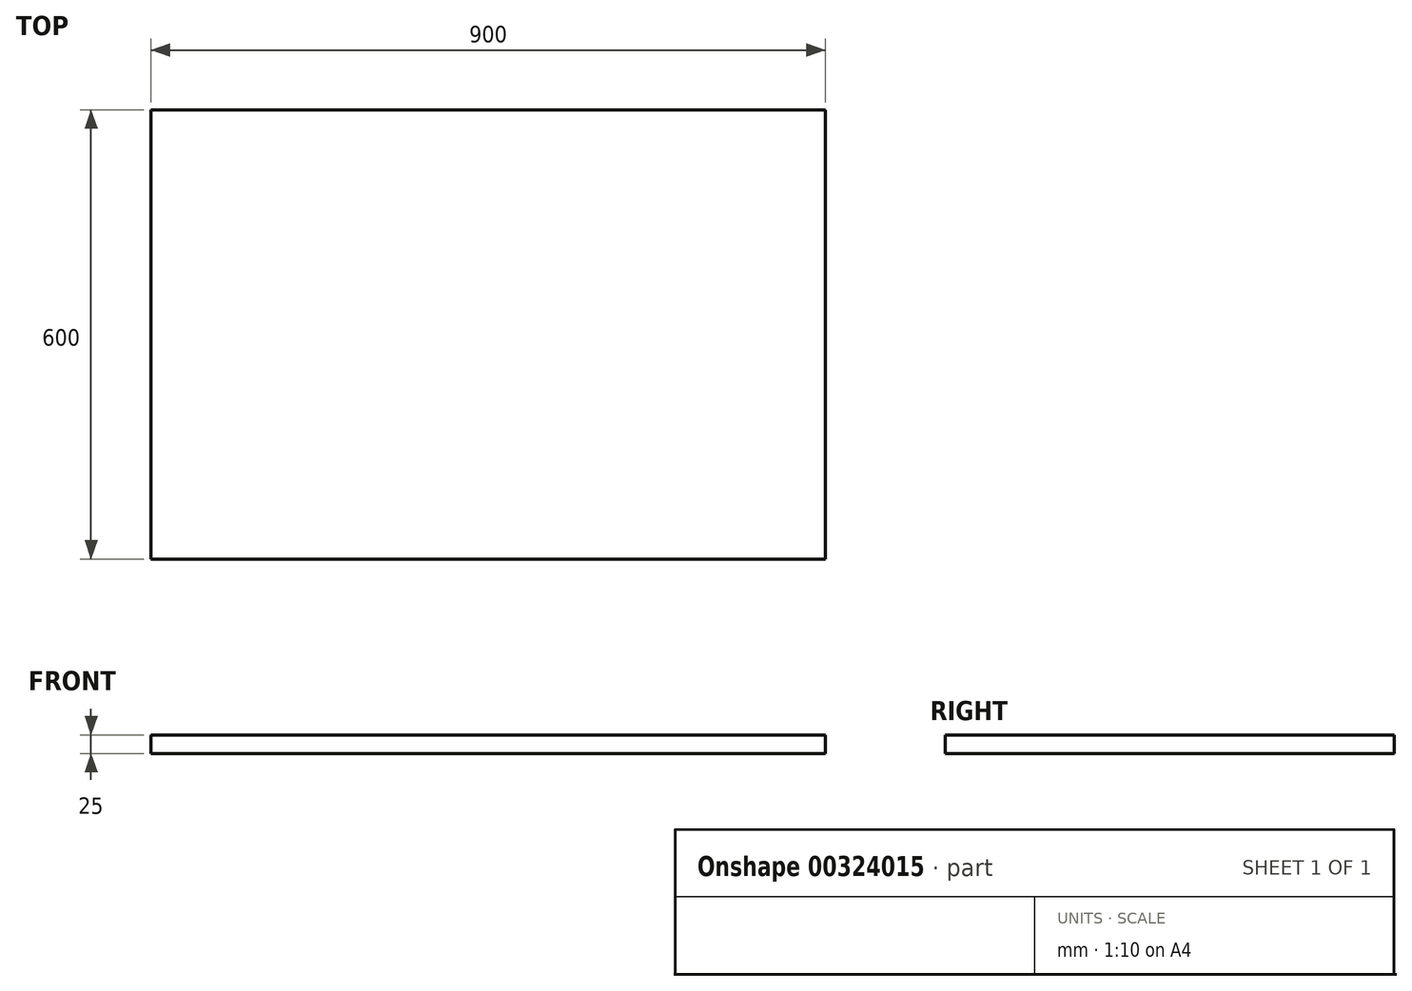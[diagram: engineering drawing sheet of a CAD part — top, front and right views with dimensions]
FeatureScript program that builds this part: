
annotation { "Feature Type Name" : "Feature", "Feature Type Description" : "" }
export const myFeature = defineFeature(function(context is Context, id is Id, definition is map)
    precondition{}
    {
        {
            var Q0;
            Q0=qCreatedBy(makeId("Top.planeOp"),FACE);
            var sketch = newSketch(context, id + "F0", { "sketchPlane" : qUnion([Q0])});
            skLineSegment(sketch, "E0.bottom", {"start": v(450, 300) * mm, "end": v(-450, 300) * mm});
            skLineSegment(sketch, "E0.top", {"start": v(450, -300) * mm, "end": v(-450, -300) * mm});
            skLineSegment(sketch, "E0.left", {"start": v(450, 300) * mm, "end": v(450, -300) * mm});
            skLineSegment(sketch, "E0.right", {"start": v(-450, 300) * mm, "end": v(-450, -300) * mm});
            skPoint(sketch, "E0.middle", {"position": v(0, 0) * mm});
            skSolve(sketch);
        }
        {
            var Q0;
            Q0=makeQuery(id+"F0.imprint","IMPRINT",FACE,{"disambiguationData":[TD([[makeQuery(id+"F0.imprint","IMPRINT",EDGE,{"derivedFrom":sQuery(id+"F0.wireOp",EDGE,"E0.bottom")}),1.0]])]});
            extrude(context, id + "F1", {"entities" : qUnion([Q0]), "depth" : 25 * mm});
        }
    });
